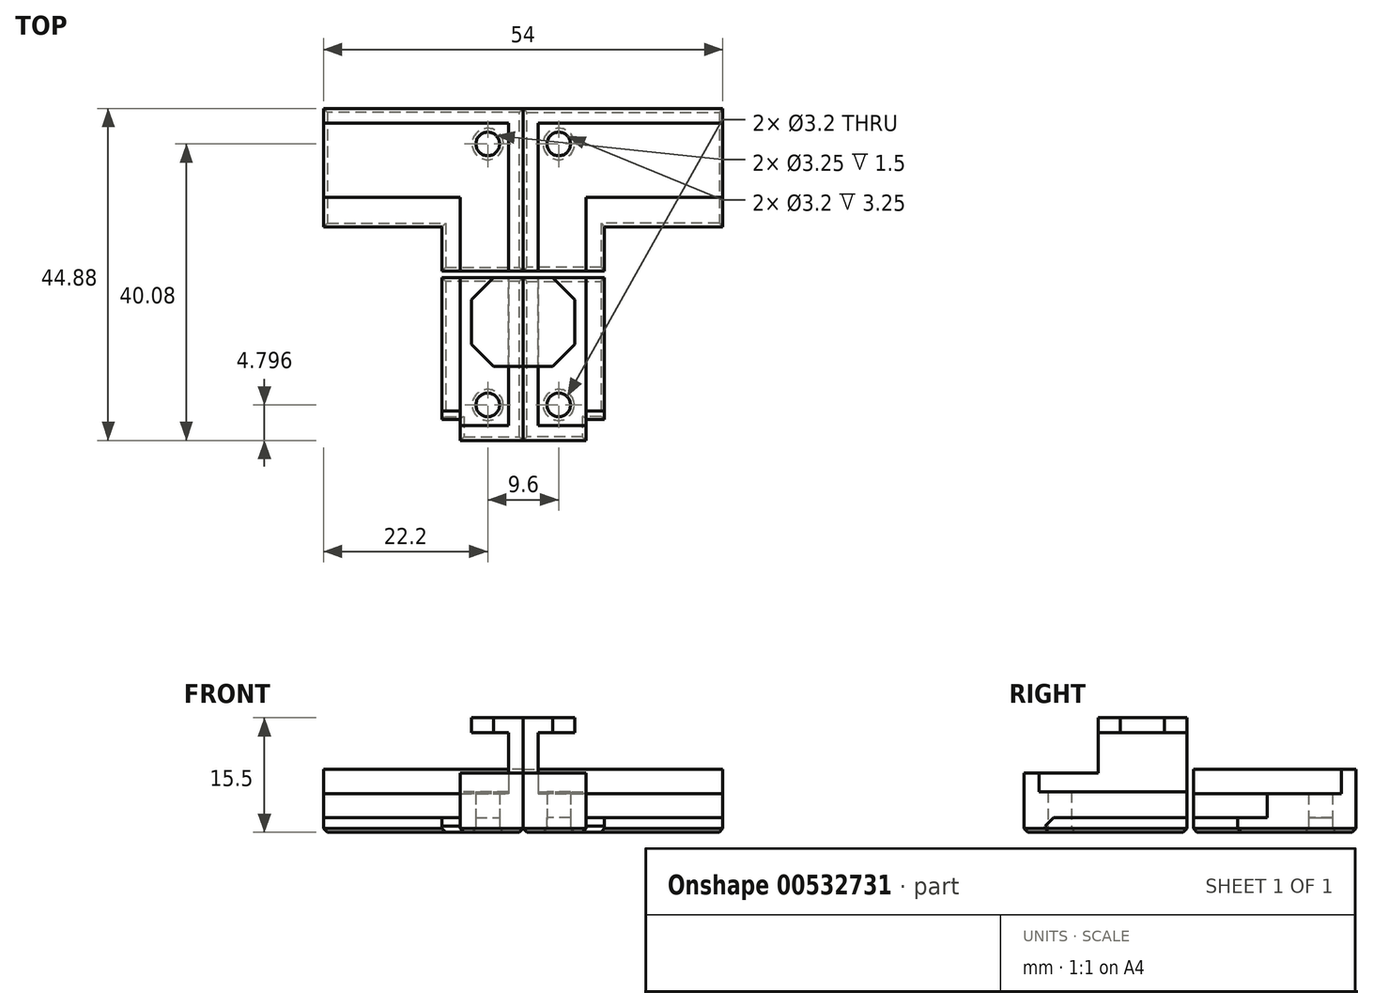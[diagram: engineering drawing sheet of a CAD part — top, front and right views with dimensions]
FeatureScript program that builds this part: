
annotation { "Feature Type Name" : "Feature", "Feature Type Description" : "" }
export const myFeature = defineFeature(function(context is Context, id is Id, definition is map)
    precondition{}
    {
        {
            var Q0;
            Q0=qCreatedBy(makeId("Top.planeOp"),FACE);
            var sketch = newSketch(context, id + "F0", { "sketchPlane" : qUnion([Q0])});
            skLineSegment(sketch, "E0", {"start": v(0, 0) * mm, "end": v(25, 0) * mm});
            skLineSegment(sketch, "E1", {"start": v(25, 0) * mm, "end": v(25, -14) * mm});
            skLineSegment(sketch, "E2", {"start": v(25, -14) * mm, "end": v(9, -14) * mm});
            skLineSegment(sketch, "E3", {"start": v(9, -14) * mm, "end": v(9, -20) * mm});
            skLineSegment(sketch, "E4", {"start": v(9, -20) * mm, "end": v(0, -20) * mm});
            skLineSegment(sketch, "E5", {"start": v(0, -20) * mm, "end": v(0, 0) * mm});
            skCircle(sketch, "E6", {"center": v(2.8, -2.8) * mm, "radius": 1.63 * mm});
            skSolve(sketch);
        }
        {
            var Q0;
            Q0 = qSketchRegion(id + "F0", true);
            extrude(context, id + "F1", {"entities" : qUnion([Q0]), "depth" : 2 * mm, "offsetDistance" : 25 * mm});
        }
        {
            var Q0;
            Q0=makeQuery(id+"F1.opExtrude","CAP_FACE",FACE,{"disambiguationData":[OSD([sQuery(id+"F0.wireOp",EDGE,"E0"),sQuery(id+"F0.wireOp",EDGE,"E1"),sQuery(id+"F0.wireOp",EDGE,"E2"),sQuery(id+"F0.wireOp",EDGE,"E3"),sQuery(id+"F0.wireOp",EDGE,"E4"),sQuery(id+"F0.wireOp",EDGE,"E5"),sQuery(id+"F0.wireOp",EDGE,"E6")])],"isStart":false});
            var sketch = newSketch(context, id + "F2", { "sketchPlane" : qUnion([Q0])});
            skCircle(sketch, "E7", {"center": v(2.8, -2.8) * mm, "radius": 1.6 * mm});
            skLineSegment(sketch, "E8", {"start": v(25, -10) * mm, "end": v(0, -10) * mm});
            skLineSegment(sketch, "E9", {"start": v(0, -10) * mm, "end": v(0, 0) * mm});
            skLineSegment(sketch, "E10", {"start": v(0, 0) * mm, "end": v(25, 0) * mm});
            skLineSegment(sketch, "E11", {"start": v(25, 0) * mm, "end": v(25, -10) * mm});
            skLineSegment(sketch, "E12.bottom", {"start": v(0, -10) * mm, "end": v(6.5, -10) * mm});
            skLineSegment(sketch, "E12.top", {"start": v(0, -20) * mm, "end": v(6.5, -20) * mm});
            skLineSegment(sketch, "E12.left", {"start": v(0, -10) * mm, "end": v(0, -20) * mm});
            skLineSegment(sketch, "E12.right", {"start": v(6.5, -10) * mm, "end": v(6.5, -20) * mm});
            skSolve(sketch);
        }
        {
            var Q0;
            Q0 = qSketchRegion(id + "F2", true);
            extrude(context, id + "F3", {"entities" : qUnion([Q0]), "operationType" : NewBodyOperationType.ADD, "depth" : 3.25 * mm, "offsetDistance" : 25 * mm});
        }
        {
            var Q0;
            Q0=makeQuery(id+"F1.opExtrude","CAP_FACE",FACE,{"disambiguationData":[OSD([sQuery(id+"F0.wireOp",EDGE,"E0"),sQuery(id+"F0.wireOp",EDGE,"E1"),sQuery(id+"F0.wireOp",EDGE,"E2"),sQuery(id+"F0.wireOp",EDGE,"E3"),sQuery(id+"F0.wireOp",EDGE,"E4"),sQuery(id+"F0.wireOp",EDGE,"E5"),sQuery(id+"F0.wireOp",EDGE,"E6")])],"isStart":true});
            var sketch = newSketch(context, id + "F4", { "sketchPlane" : qUnion([Q0])});
            skLineSegment(sketch, "E13", {"start": v(25, 0) * mm, "end": v(25, -2) * mm});
            skLineSegment(sketch, "E14", {"start": v(25, -2) * mm, "end": v(-2, -2) * mm});
            skLineSegment(sketch, "E15", {"start": v(-2, -2) * mm, "end": v(-2, 20) * mm});
            skLineSegment(sketch, "E16", {"start": v(-2, 20) * mm, "end": v(0, 20) * mm});
            skLineSegment(sketch, "E17", {"start": v(25, 0) * mm, "end": v(0, 0) * mm});
            skLineSegment(sketch, "E18", {"start": v(0, 0) * mm, "end": v(0, 20) * mm});
            skSolve(sketch);
        }
        {
            var Q0;
            Q0 = qSketchRegion(id + "F4", true);
            extrude(context, id + "F5", {"entities" : qUnion([Q0]), "operationType" : NewBodyOperationType.ADD, "oppositeDirection" : true, "depth" : 8.5 * mm, "offsetDistance" : 25 * mm});
        }
        {
            var Q0;
            Q0=qCreatedBy(makeId("Top.planeOp"),FACE);
            var sketch = newSketch(context, id + "F6", { "sketchPlane" : qUnion([Q0])});
            skLineSegment(sketch, "E19.bottom", {"start": v(0, -20.88) * mm, "end": v(9, -20.88) * mm});
            skLineSegment(sketch, "E19.top", {"start": v(0, -40.88) * mm, "end": v(9, -40.88) * mm});
            skLineSegment(sketch, "E19.left", {"start": v(0, -20.88) * mm, "end": v(0, -40.88) * mm});
            skLineSegment(sketch, "E19.right", {"start": v(9, -20.88) * mm, "end": v(9, -40.88) * mm});
            skSolve(sketch);
        }
        {
            var Q0;
            Q0=makeQuery(id+"F6.imprint","IMPRINT",FACE,{"disambiguationData":[TD([[makeQuery(id+"F6.imprint","IMPRINT",EDGE,{"derivedFrom":sQuery(id+"F6.wireOp",EDGE,"E19.bottom")}),-1.0]])]});
            extrude(context, id + "F7", {"entities" : qUnion([Q0]), "depth" : 2 * mm, "offsetDistance" : 25 * mm});
        }
        {
            var Q0;
            Q0=makeQuery(id+"F7.opExtrude","CAP_FACE",FACE,{"disambiguationData":[OSD([sQuery(id+"F6.wireOp",EDGE,"E19.bottom"),sQuery(id+"F6.wireOp",EDGE,"E19.top"),sQuery(id+"F6.wireOp",EDGE,"E19.left"),sQuery(id+"F6.wireOp",EDGE,"E19.right")])],"isStart":false});
            var sketch = newSketch(context, id + "F8", { "sketchPlane" : qUnion([Q0])});
            skLineSegment(sketch, "E20.bottom", {"start": v(0, -20.88) * mm, "end": v(6.5, -20.88) * mm});
            skLineSegment(sketch, "E20.top", {"start": v(0, -40.88) * mm, "end": v(6.5, -40.88) * mm});
            skLineSegment(sketch, "E20.left", {"start": v(0, -20.88) * mm, "end": v(0, -40.88) * mm});
            skLineSegment(sketch, "E20.right", {"start": v(6.5, -20.88) * mm, "end": v(6.5, -40.88) * mm});
            skSolve(sketch);
        }
        {
            var Q0;
            Q0=makeQuery(id+"F8.imprint","IMPRINT",FACE,{"disambiguationData":[TD([[makeQuery(id+"F8.imprint","IMPRINT",EDGE,{"derivedFrom":sQuery(id+"F8.wireOp",EDGE,"E20.bottom")}),-1.0]])]});
            extrude(context, id + "F9", {"entities" : qUnion([Q0]), "operationType" : NewBodyOperationType.ADD, "depth" : 3.5 * mm, "offsetDistance" : 25 * mm});
        }
        {
            var Q0;
            Q0=makeQuery(id+"F7.opExtrude","CAP_FACE",FACE,{"disambiguationData":[OSD([sQuery(id+"F6.wireOp",EDGE,"E19.bottom"),sQuery(id+"F6.wireOp",EDGE,"E19.top"),sQuery(id+"F6.wireOp",EDGE,"E19.left"),sQuery(id+"F6.wireOp",EDGE,"E19.right")])],"isStart":true});
            var sketch = newSketch(context, id + "F10", { "sketchPlane" : qUnion([Q0])});
            skLineSegment(sketch, "E21", {"start": v(0, 20.88) * mm, "end": v(-2, 20.88) * mm});
            skLineSegment(sketch, "E22", {"start": v(-2, 20.88) * mm, "end": v(-2, 42.88) * mm});
            skLineSegment(sketch, "E23", {"start": v(-2, 42.88) * mm, "end": v(6.5, 42.88) * mm});
            skLineSegment(sketch, "E24", {"start": v(6.5, 42.88) * mm, "end": v(6.5, 40.88) * mm});
            skLineSegment(sketch, "E25", {"start": v(0, 20.88) * mm, "end": v(0, 40.88) * mm});
            skLineSegment(sketch, "E26", {"start": v(0, 40.88) * mm, "end": v(6.5, 40.88) * mm});
            skLineSegment(sketch, "E27", {"start": v(0, 40.88) * mm, "end": v(-2, 40.88) * mm});
            skLineSegment(sketch, "E28", {"start": v(-2, 32.88) * mm, "end": v(0, 32.88) * mm});
            skSolve(sketch);
        }
        {
            var Q0;
            Q0=makeQuery(id+"F10.imprint","IMPRINT",FACE,{"disambiguationData":[TD([[makeQuery(id+"F10.imprint","IMPRINT",EDGE,{"derivedFrom":sQuery(id+"F10.wireOp",EDGE,"E21")}),-1.0]])]});
            extrude(context, id + "F11", {"entities" : qUnion([Q0]), "operationType" : NewBodyOperationType.ADD, "oppositeDirection" : true, "depth" : 15.5 * mm, "offsetDistance" : 25 * mm});
        }
        {
            var Q0;
            {var subQ0=sQuery(id+"F10.wireOp",EDGE,"E23");Q0=makeQuery(id+"F10.imprint","IMPRINT",FACE,{"disambiguationData":[TD([[makeQuery(id+"F10.imprint","IMPRINT",EDGE,{"derivedFrom":subQ0}),-1.0]])]});}
            var Q1;
            {var subQ0=sQuery(id+"F10.wireOp",EDGE,"E27");Q1=makeQuery(id+"F10.imprint","IMPRINT",FACE,{"disambiguationData":[TD([[makeQuery(id+"F10.imprint","IMPRINT",EDGE,{"derivedFrom":subQ0}),1.0]])]});}
            extrude(context, id + "F12", {"entities" : qUnion([Q0, Q1]), "operationType" : NewBodyOperationType.ADD, "oppositeDirection" : true, "depth" : 8 * mm, "offsetDistance" : 25 * mm});
        }
        {
            var Q0;
            Q0=makeQuery(id+"F11.opExtrude","SWEPT_FACE",FACE,{"disambiguationData":[OSD([sQuery(id+"F10.wireOp",EDGE,"E25")])]});
            var sketch = newSketch(context, id + "F13", { "sketchPlane" : qUnion([Q0])});
            skLineSegment(sketch, "E29.bottom", {"start": v(-32.88, 15.5) * mm, "end": v(-20.88, 15.5) * mm});
            skLineSegment(sketch, "E29.top", {"start": v(-32.88, 13.5) * mm, "end": v(-20.88, 13.5) * mm});
            skLineSegment(sketch, "E29.left", {"start": v(-32.88, 15.5) * mm, "end": v(-32.88, 13.5) * mm});
            skLineSegment(sketch, "E29.right", {"start": v(-20.88, 15.5) * mm, "end": v(-20.88, 13.5) * mm});
            skSolve(sketch);
        }
        {
            var Q0;
            Q0 = qSketchRegion(id + "F13", true);
            extrude(context, id + "F14", {"entities" : qUnion([Q0]), "operationType" : NewBodyOperationType.ADD, "depth" : 5 * mm, "offsetDistance" : 25 * mm});
        }
        {
            var Q0;
            Q0=makeQuery(id+"F14.opExtrude","CAP_EDGE",EDGE,{"disambiguationData":[OSD([sQuery(id+"F13.wireOp",EDGE,"E29.right")])],"isStart":false});
            var Q1;
            Q1=makeQuery(id+"F14.opExtrude","CAP_EDGE",EDGE,{"disambiguationData":[OSD([sQuery(id+"F13.wireOp",EDGE,"E29.left")])],"isStart":false});
            chamfer(context, id + "F15", {"entities" : qUnion([Q0, Q1]), "width" : 3 * mm, "tangentPropagation" : true});
        }
        {
            var Q0;
            {var subQ0=sQuery(id+"F10.wireOp",EDGE,"E26");Q0=makeQuery(id+"F10.imprint","IMPRINT",FACE,{"disambiguationData":[TD([[makeQuery(id+"F10.imprint","IMPRINT",EDGE,{"derivedFrom":subQ0}),-1.0]])]});}
            var sketch = newSketch(context, id + "F16", { "sketchPlane" : qUnion([Q0])});
            skCircle(sketch, "E30", {"center": v(2.8, 38.08) * mm, "radius": 1.6 * mm});
            skSolve(sketch);
        }
        {
            var Q0;
            Q0 = qSketchRegion(id + "F16", true);
            extrude(context, id + "F17", {"entities" : qUnion([Q0]), "operationType" : NewBodyOperationType.REMOVE, "endBound" : BoundingType.UP_TO_NEXT, "oppositeDirection" : true, "depth" : 25 * mm, "offsetDistance" : 25 * mm});
        }
        {
            var Q0;
            Q0=makeQuery(id+"F7.opExtrude","CAP_EDGE",EDGE,{"disambiguationData":[OSD([sQuery(id+"F6.wireOp",EDGE,"E19.top")])],"isStart":false});
            chamfer(context, id + "F18", {"entities" : qUnion([Q0]), "width" : 2 * mm, "tangentPropagation" : true});
        }
        {
            var Q0;
            Q0=makeQuery(id+"FVV7asG2V6Blrpq_1.boolean.opBoolean","COPY",EDGE,{"derivedFrom":makeQuery(id+"FVV7asG2V6Blrpq_1.opExtrude","CAP_EDGE",EDGE,{"disambiguationData":[OSD([sQuery(id+"FQpcZ8dMN0XivS9_1.wireOp",EDGE,"hSKNbRGm-mt8F-bVzb-eotC-35c6e9DlgVQ2")])],"isStart":true})});
            var Q1;
            Q1=makeQuery(id+"F5.boolean.opBoolean","MERGE",FACE,{"derivedFrom":[makeQuery(id+"F1.opExtrude","CAP_FACE",FACE,{"disambiguationData":[OSD([sQuery(id+"F0.wireOp",EDGE,"E0"),sQuery(id+"F0.wireOp",EDGE,"E1"),sQuery(id+"F0.wireOp",EDGE,"E2"),sQuery(id+"F0.wireOp",EDGE,"E3"),sQuery(id+"F0.wireOp",EDGE,"E4"),sQuery(id+"F0.wireOp",EDGE,"E5"),sQuery(id+"F0.wireOp",EDGE,"E6")])],"isStart":true}),makeQuery(id+"F5.opExtrude","CAP_FACE",FACE,{"disambiguationData":[OSD([sQuery(id+"F4.wireOp",EDGE,"E13"),sQuery(id+"F4.wireOp",EDGE,"E14"),sQuery(id+"F4.wireOp",EDGE,"E15"),sQuery(id+"F4.wireOp",EDGE,"E16"),sQuery(id+"F4.wireOp",EDGE,"E17"),sQuery(id+"F4.wireOp",EDGE,"E18")])],"isStart":true})]});
            var Q2;
            {var subQ0=sQuery(id+"F10.wireOp",EDGE,"E28");var subQ1=sQuery(id+"F10.wireOp",EDGE,"E25");var subQ2=sQuery(id+"F10.wireOp",EDGE,"E22");Q2=makeQuery(id+"F12.boolean.opBoolean","MERGE",FACE,{"derivedFrom":[makeQuery(id+"F11.boolean.opBoolean","MERGE",FACE,{"derivedFrom":[makeQuery(id+"F7.opExtrude","CAP_FACE",FACE,{"disambiguationData":[OSD([sQuery(id+"F6.wireOp",EDGE,"E19.bottom"),sQuery(id+"F6.wireOp",EDGE,"E19.top"),sQuery(id+"F6.wireOp",EDGE,"E19.left"),sQuery(id+"F6.wireOp",EDGE,"E19.right")])],"isStart":true}),makeQuery(id+"F11.opExtrude","CAP_FACE",FACE,{"disambiguationData":[OSD([sQuery(id+"F10.wireOp",EDGE,"E21"),subQ2,subQ1,subQ0])],"isStart":true})]}),makeQuery(id+"F12.opExtrude","CAP_FACE",FACE,{"disambiguationData":[OSD([subQ2,sQuery(id+"F10.wireOp",EDGE,"E23"),sQuery(id+"F10.wireOp",EDGE,"E24"),subQ1,sQuery(id+"F10.wireOp",EDGE,"E26"),subQ0])],"isStart":true})]});}
            chamfer(context, id + "F19", {"entities" : qUnion([Q0, Q1, Q2]), "width" : 0.5 * mm, "tangentPropagation" : true});
        }
        {
            var Q0;
            Q0=makeQuery(id+"F1.opExtrude","SWEPT_BODY",BODY,{"disambiguationData":[OSD([sQuery(id+"F0.wireOp",EDGE,"E0"),sQuery(id+"F0.wireOp",EDGE,"E1"),sQuery(id+"F0.wireOp",EDGE,"E2"),sQuery(id+"F0.wireOp",EDGE,"E3"),sQuery(id+"F0.wireOp",EDGE,"E4"),sQuery(id+"F0.wireOp",EDGE,"E5"),sQuery(id+"F0.wireOp",EDGE,"E6")])]});
            var Q1;
            Q1=makeQuery(id+"F7.opExtrude","SWEPT_BODY",BODY,{"disambiguationData":[OSD([sQuery(id+"F6.wireOp",EDGE,"E19.bottom"),sQuery(id+"F6.wireOp",EDGE,"E19.top"),sQuery(id+"F6.wireOp",EDGE,"E19.left"),sQuery(id+"F6.wireOp",EDGE,"E19.right")])]});
            var Q2;
            Q2=makeQuery(id+"F5.opExtrude","SWEPT_FACE",FACE,{"disambiguationData":[OSD([sQuery(id+"F4.wireOp",EDGE,"E15")])]});
            mirror(context, id + "F20", {"entities" : qUnion([Q0, Q1]), "mirrorPlane" : qUnion([Q2])});
        }
    });
